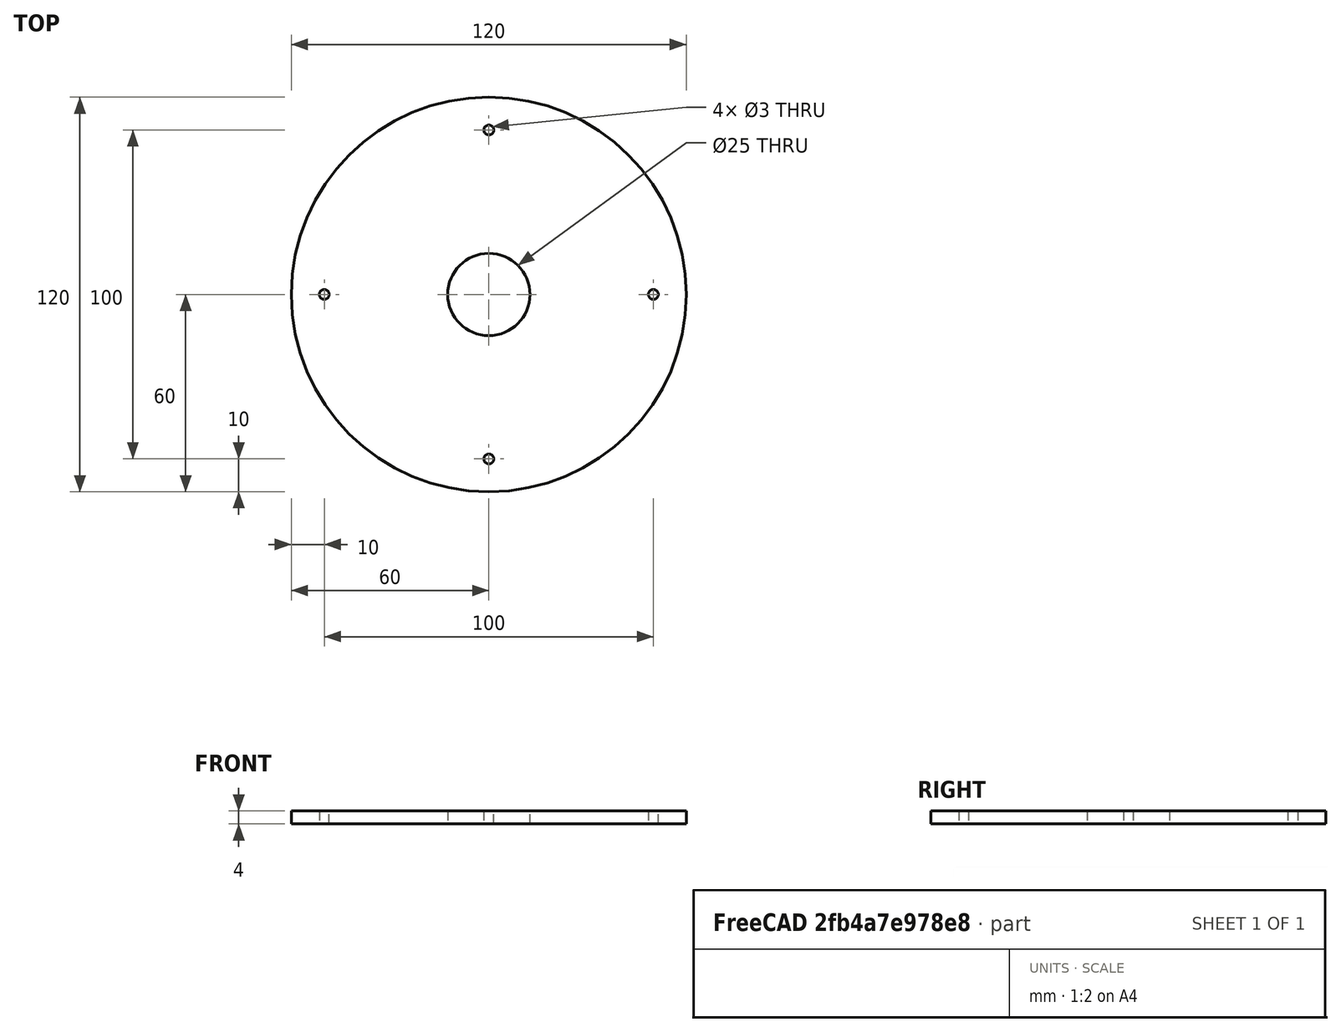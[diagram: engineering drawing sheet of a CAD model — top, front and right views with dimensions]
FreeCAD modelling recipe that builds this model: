
FCSTD DOCUMENT  (FreeCAD 0.19R24276 (Git))
Label: circle_seal_holder_part1
License: All rights reserved
LicenseURL: http://en.wikipedia.org/wiki/All_rights_reserved
objects: Sketcher::SketchObject×1, PartDesign::Pad×1, PartDesign::Body×1
note: 4 computed .brp shape members not serialized (recipe doc carries the construction recipe); baked Part::Feature solids carry a one-line shape summary decoded from their .brp

FEATURE [Sketcher::SketchObject] Sketch
  FullyConstrained = true
  MapMode = 5
  Support = -> [XY_Plane]
  sketch-geometry (11):
    g0: Circle CenterX=0 CenterY=0 CenterZ=0 NormalX=0 NormalY=0 NormalZ=1 AngleXU=0 Radius=12.5
    g1: Circle CenterX=0 CenterY=0 CenterZ=0 NormalX=0 NormalY=0 NormalZ=1 AngleXU=0 Radius=60
    g2: Circle CenterX=0 CenterY=50 CenterZ=0 NormalX=0 NormalY=0 NormalZ=1 AngleXU=0 Radius=1.5
    g3: Circle CenterX=0 CenterY=-50 CenterZ=0 NormalX=0 NormalY=0 NormalZ=1 AngleXU=0 Radius=1.5
    g4: Circle CenterX=50 CenterY=0 CenterZ=0 NormalX=0 NormalY=0 NormalZ=1 AngleXU=0 Radius=1.5
    g5: Circle CenterX=-50 CenterY=0 CenterZ=0 NormalX=0 NormalY=0 NormalZ=1 AngleXU=0 Radius=1.5
    g6: Circle CenterX=0 CenterY=0 CenterZ=0 NormalX=0 NormalY=0 NormalZ=1 AngleXU=0 Radius=50
    g7: LineSegment StartX=0 StartY=0 StartZ=0 EndX=-50 EndY=0 EndZ=0
    g8: LineSegment StartX=0 StartY=0 StartZ=0 EndX=0 EndY=50 EndZ=0
    g9: LineSegment StartX=0 StartY=0 StartZ=0 EndX=50 EndY=0 EndZ=0
    g10: LineSegment StartX=0 StartY=0 StartZ=0 EndX=0 EndY=-50 EndZ=0
  constraints (26):
    c: Coincident(g0,g-1)
    c: Diameter(g0) = 25
    c: Coincident(g1,g0)
    c: Diameter(g1) = 120
    c: PointOnObject(g2,g-2)
    c: PointOnObject(g3,g-2)
    c: PointOnObject(g4,g-1)
    c: PointOnObject(g5,g-1)
    c: Diameter(g2) = 3
    c: Equal(g2,g5)
    c: Equal(g2,g3)
    c: Equal(g2,g4)
    c: Coincident(g6,g0)
    c: Coincident(g7,g0)
    c: Coincident(g8,g0)
    c: Coincident(g9,g0)
    c: Coincident(g10,g0)
    c: PointOnObject(g10,g6)
    c: PointOnObject(g7,g6)
    c: PointOnObject(g8,g6)
    c: PointOnObject(g9,g6)
    c: Coincident(g5,g7)
    c: Coincident(g2,g8)
    c: Coincident(g4,g9)
    c: Coincident(g3,g10)
    c: Diameter(g6) = 100  '1'
FEATURE [PartDesign::Pad] Pad
  Direction = (1,1,1)
  Length = 4
  Length2 = 100
  Profile = -> Sketch
  Type = 0
FEATURE [PartDesign::Body] Body
  Group = -> [Sketch,Pad]
  Origin = -> Origin
  Tip = -> Pad
